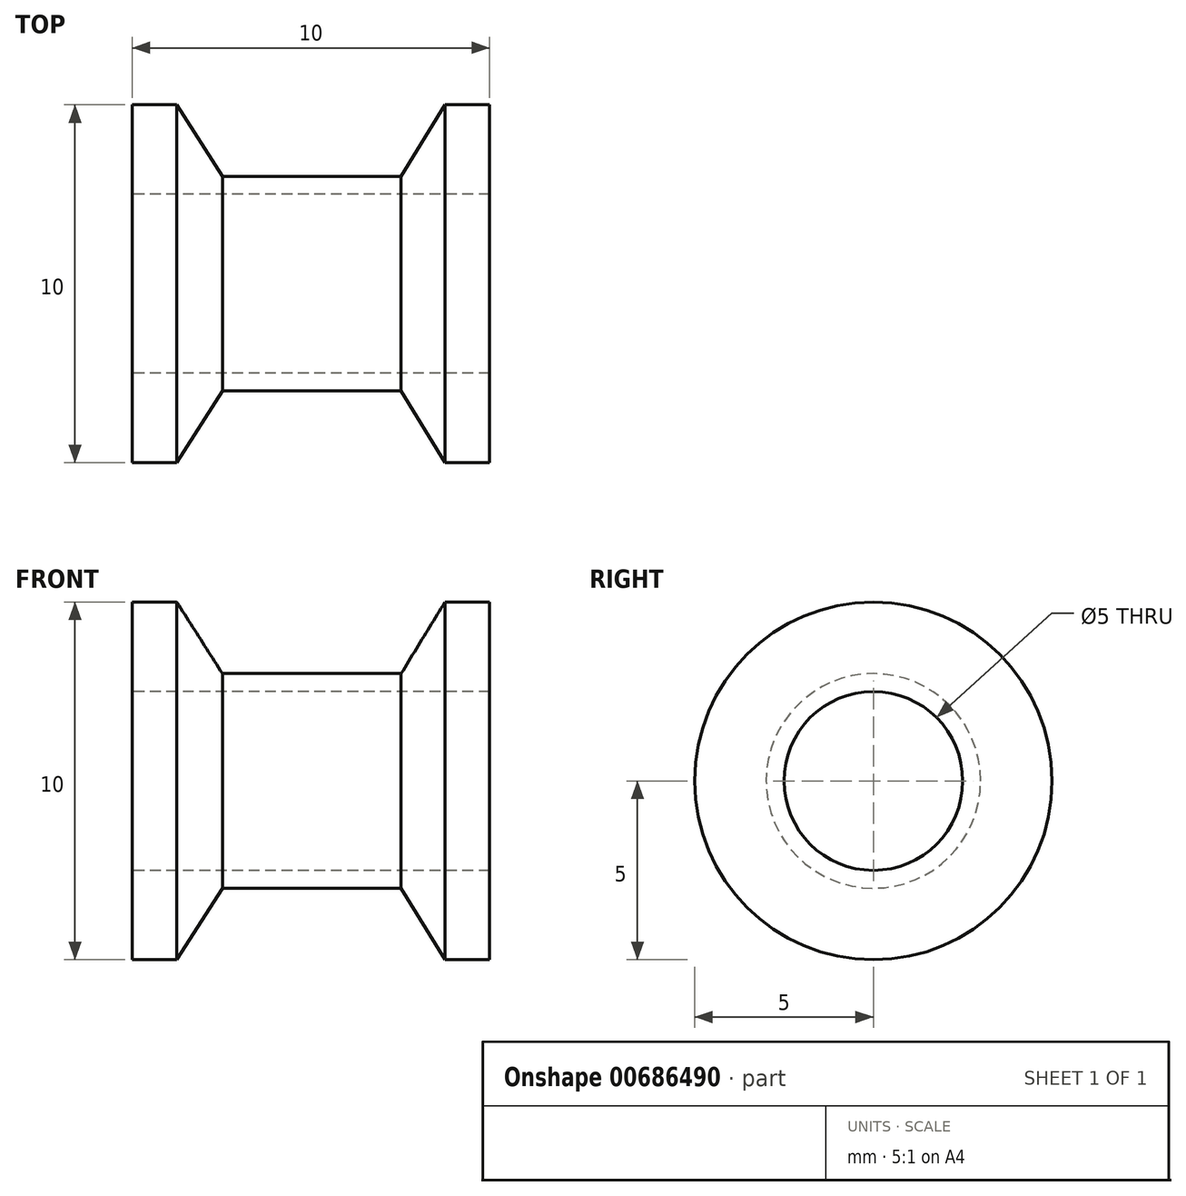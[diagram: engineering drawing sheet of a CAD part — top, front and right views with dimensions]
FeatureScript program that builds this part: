
annotation { "Feature Type Name" : "Feature", "Feature Type Description" : "" }
export const myFeature = defineFeature(function(context is Context, id is Id, definition is map)
    precondition{}
    {
        {
            var Q0;
            Q0=qCreatedBy(makeId("Front.planeOp"),FACE);
            var sketch = newSketch(context, id + "F0", { "sketchPlane" : qUnion([Q0])});
            skLineSegment(sketch, "E0.bottom", {"start": v(-5, 0) * mm, "end": v(5, 0) * mm});
            skLineSegment(sketch, "E0.left", {"start": v(-5, 0) * mm, "end": v(-5, 2.5) * mm});
            skLineSegment(sketch, "E0.right", {"start": v(5, 0) * mm, "end": v(5, 2.5) * mm});
            skLineSegment(sketch, "E1", {"start": v(-2.48, 0.5) * mm, "end": v(2.52, 0.5) * mm});
            skLineSegment(sketch, "E2", {"start": v(-14.94, -2.5) * mm, "end": v(21.37, -2.5) * mm});
            skLineSegment(sketch, "E3", {"start": v(-5, 2.5) * mm, "end": v(-3.75, 2.5) * mm});
            skLineSegment(sketch, "E4", {"start": v(-3.75, 2.5) * mm, "end": v(-2.48, 0.5) * mm});
            skLineSegment(sketch, "E5", {"start": v(2.52, 0.5) * mm, "end": v(3.75, 2.5) * mm});
            skLineSegment(sketch, "E6", {"start": v(3.75, 2.5) * mm, "end": v(5, 2.5) * mm});
            skSolve(sketch);
        }
        {
            var Q0;
            Q0=makeQuery(id+"F0.imprint","IMPRINT",FACE,{"disambiguationData":[TD([[makeQuery(id+"F0.imprint","IMPRINT",EDGE,{"derivedFrom":sQuery(id+"F0.wireOp",EDGE,"E0.bottom")}),1.0]])]});
            var Q1;
            Q1=sQuery(id+"F0.wireOp",EDGE,"E2");
            revolve(context, id + "F1", {"entities" : qUnion([Q0]), "axis" : qUnion([Q1]), "revolveType" : RevolveType.FULL});
        }
    });
